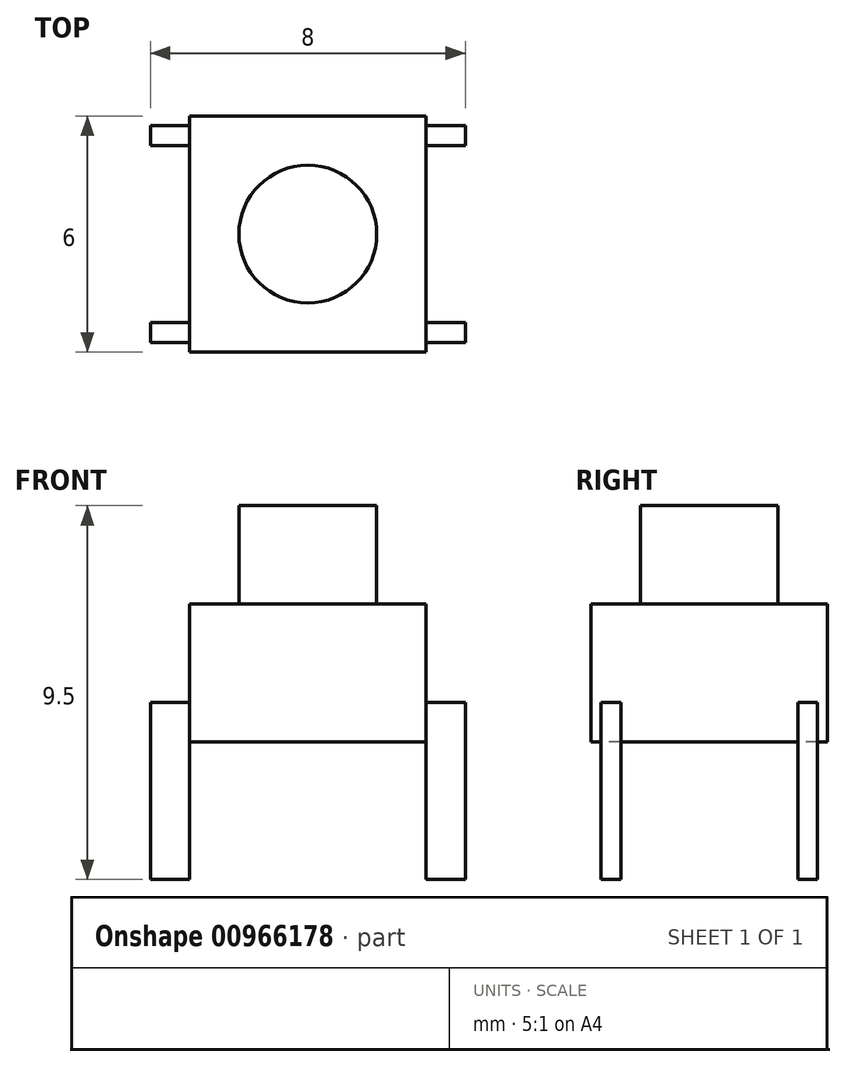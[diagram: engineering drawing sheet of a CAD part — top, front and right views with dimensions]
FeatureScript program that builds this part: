
annotation { "Feature Type Name" : "Feature", "Feature Type Description" : "" }
export const myFeature = defineFeature(function(context is Context, id is Id, definition is map)
    precondition{}
    {
        {
            var Q0;
            Q0=qCreatedBy(makeId("Top.planeOp"),FACE);
            var sketch = newSketch(context, id + "F0", { "sketchPlane" : qUnion([Q0])});
            skLineSegment(sketch, "E0.bottom", {"start": v(3, 3) * mm, "end": v(-3, 3) * mm});
            skLineSegment(sketch, "E0.top", {"start": v(3, -3) * mm, "end": v(-3, -3) * mm});
            skLineSegment(sketch, "E0.left", {"start": v(3, 3) * mm, "end": v(3, -3) * mm});
            skLineSegment(sketch, "E0.right", {"start": v(-3, 3) * mm, "end": v(-3, -3) * mm});
            skPoint(sketch, "E0.middle", {"position": v(0, 0) * mm});
            skCircle(sketch, "E1", {"center": v(0, 0) * mm, "radius": 1.75 * mm});
            skLineSegment(sketch, "E2.bottom", {"start": v(3, 2.75) * mm, "end": v(4, 2.75) * mm});
            skLineSegment(sketch, "E2.top", {"start": v(3, 2.25) * mm, "end": v(4, 2.25) * mm});
            skLineSegment(sketch, "E2.left", {"start": v(3, 2.75) * mm, "end": v(3, 2.25) * mm});
            skLineSegment(sketch, "E2.right", {"start": v(4, 2.75) * mm, "end": v(4, 2.25) * mm});
            skLineSegment(sketch, "E3.MirrorCS", {"start": v(3, -2.25) * mm, "end": v(4, -2.25) * mm});
            skLineSegment(sketch, "E4.MirrorCS", {"start": v(4, -2.75) * mm, "end": v(4, -2.25) * mm});
            skLineSegment(sketch, "E5.MirrorCS", {"start": v(3, -2.75) * mm, "end": v(4, -2.75) * mm});
            skLineSegment(sketch, "E6.MirrorCS", {"start": v(-3, -2.75) * mm, "end": v(-4, -2.75) * mm});
            skLineSegment(sketch, "E7.MirrorCS", {"start": v(-4, -2.75) * mm, "end": v(-4, -2.25) * mm});
            skLineSegment(sketch, "E8.MirrorCS", {"start": v(-3, -2.25) * mm, "end": v(-4, -2.25) * mm});
            skLineSegment(sketch, "E9.MirrorCS", {"start": v(-3, 2.25) * mm, "end": v(-4, 2.25) * mm});
            skLineSegment(sketch, "E10.MirrorCS", {"start": v(-3, 2.75) * mm, "end": v(-4, 2.75) * mm});
            skLineSegment(sketch, "E11.MirrorCS", {"start": v(-4, 2.75) * mm, "end": v(-4, 2.25) * mm});
            skSolve(sketch);
        }
        {
            var Q0;
            {var subQ8=sQuery(id+"F0.wireOp",EDGE,"E0.bottom");Q0=makeQuery(id+"F0.imprint","IMPRINT",FACE,{"disambiguationData":[TD([[makeQuery(id+"F0.imprint","IMPRINT",EDGE,{"derivedFrom":subQ8}),1.0]])]});}
            extrude(context, id + "F1", {"entities" : qUnion([Q0]), "depth" : 3.5 * mm, "offsetDistance" : 25 * mm});
        }
        {
            var Q0;
            Q0=makeQuery(id+"F0.imprint","IMPRINT",FACE,{"disambiguationData":[TD([[makeQuery(id+"F0.imprint","IMPRINT",EDGE,{"derivedFrom":sQuery(id+"F0.wireOp",EDGE,"E1")}),1.0]])]});
            extrude(context, id + "F2", {"entities" : qUnion([Q0]), "operationType" : NewBodyOperationType.ADD, "depth" : 6 * mm, "offsetDistance" : 25 * mm});
        }
        {
            var Q0;
            {var subQ0=sQuery(id+"F0.wireOp",EDGE,"E6.MirrorCS");Q0=makeQuery(id+"F0.imprint","IMPRINT",FACE,{"disambiguationData":[TD([[makeQuery(id+"F0.imprint","IMPRINT",EDGE,{"derivedFrom":subQ0}),-1.0]])]});}
            var Q1;
            {var subQ0=sQuery(id+"F0.wireOp",EDGE,"E9.MirrorCS");Q1=makeQuery(id+"F0.imprint","IMPRINT",FACE,{"disambiguationData":[TD([[makeQuery(id+"F0.imprint","IMPRINT",EDGE,{"derivedFrom":subQ0}),-1.0]])]});}
            var Q2;
            {var subQ2=sQuery(id+"F0.wireOp",EDGE,"E2.bottom");Q2=makeQuery(id+"F0.imprint","IMPRINT",FACE,{"disambiguationData":[TD([[makeQuery(id+"F0.imprint","IMPRINT",EDGE,{"derivedFrom":subQ2}),-1.0]])]});}
            var Q3;
            {var subQ0=sQuery(id+"F0.wireOp",EDGE,"E3.MirrorCS");Q3=makeQuery(id+"F0.imprint","IMPRINT",FACE,{"disambiguationData":[TD([[makeQuery(id+"F0.imprint","IMPRINT",EDGE,{"derivedFrom":subQ0}),-1.0]])]});}
            extrude(context, id + "F3", {"entities" : qUnion([Q0, Q1, Q2, Q3]), "operationType" : NewBodyOperationType.ADD, "depth" : 1 * mm, "offsetDistance" : 25 * mm, "hasSecondDirection" : true, "secondDirectionOppositeDirection" : true, "secondDirectionDepth" : 3.5 * mm});
        }
    });
